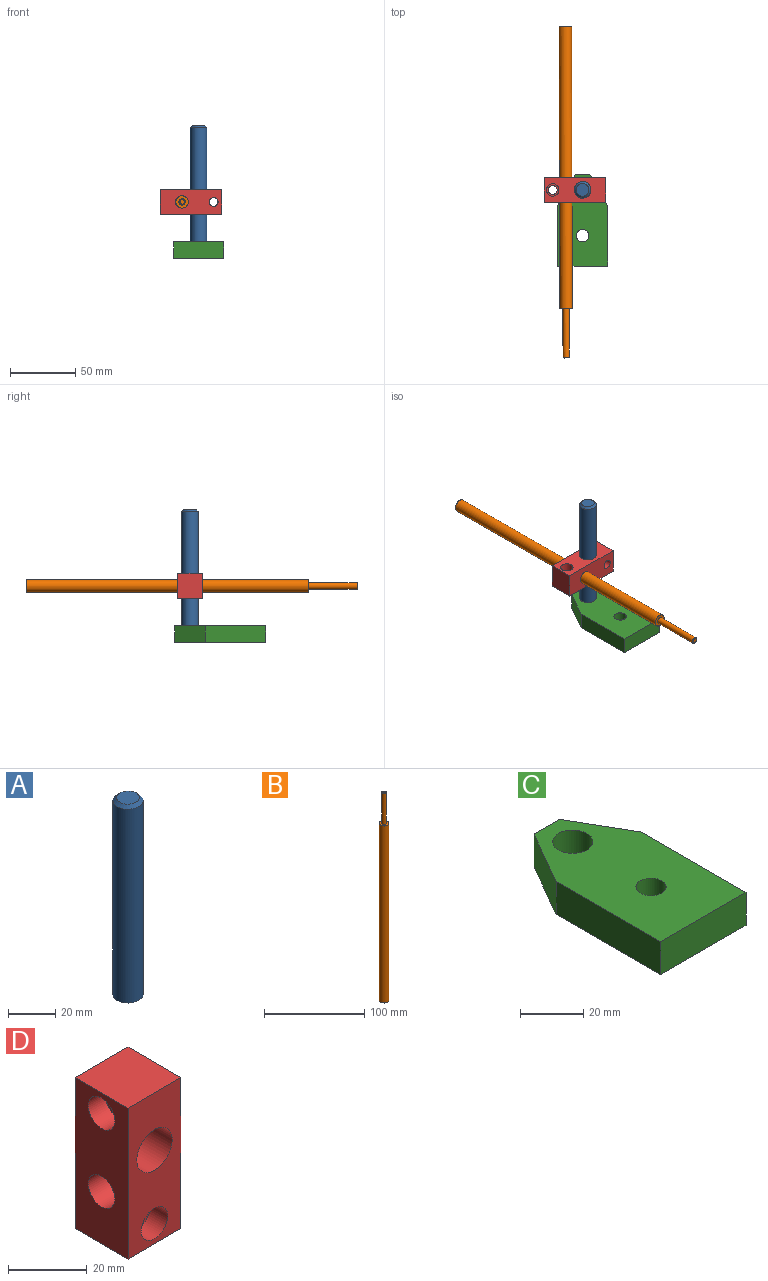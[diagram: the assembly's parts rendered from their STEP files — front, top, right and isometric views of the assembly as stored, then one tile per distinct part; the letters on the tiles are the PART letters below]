
ASSEMBLY  parts=4 mates=4
PART A: 4 faces, bbox 12.7x12.7x101.6 mm
  f0: cylinder r=6.35mm len=100.08mm, axis (0,0,-1), area 3992.9mm2, adj f2,f3
  f1: plane 9.65x9.65mm, normal (0,0,1), area 73.2mm2, adj f3
  f2: plane 12.7x12.7mm, normal (0,0,-1), area 126.7mm2, adj f0
  f3: cone r=4.83mm half-angle=45deg, axis (0,0,-1), area 75.7mm2, adj f0,f1
PART B: 6 faces, bbox 9.5x9.5x254 mm
  f0: cylinder r=4.76mm len=215.9mm, axis (0,0,-1), area 6460.5mm2, adj f1,f2
  f1: plane 9.53x9.53mm, normal (0,0,1), area 53.4mm2, adj f0,f3
  f2: plane 9.53x9.53mm, normal (0,0,-1), area 71.3mm2, adj f0
  f3: cylinder r=2.38mm len=37.47mm, axis (0,0,-1), area 560.5mm2, adj f1,f5
  f4: plane 3.49x3.49mm, normal (0,0,1), area 9.6mm2, adj f5
  f5: cone r=1.75mm half-angle=45deg, axis (0,0,-1), area 11.6mm2, adj f3,f4
PART C: 10 faces, bbox 38.1x69.8x12.7 mm
  f0: plane 46.57x12.7mm, normal (-1,0,0), area 591.4mm2, adj f1,f7,f8,f9
  f1: plane 38.1x12.7mm, normal (0,-1,0), area 483.9mm2, adj f0,f2,f8,f9
  f2: plane 46.57x12.7mm, normal (1,0,0), area 591.4mm2, adj f1,f3,f8,f9
  f3: plane 23.27x13.44mm, normal (0.87,0.5,0), area 341.3mm2, adj f2,f4,f8,f9
  f4: plane 12.7x11.23mm, normal (0,1,0), area 142.6mm2, adj f3,f7,f8,f9
  f5: cylinder r=4.76mm len=12.7mm, axis (0,0,-1), area 380mm2, adj f8,f9
  f6: cylinder r=6.35mm len=12.7mm, axis (0,0,-1), area 506.7mm2, adj f8,f9
  f7: plane 23.27x13.44mm, normal (-0.87,0.5,0), area 341.3mm2, adj f0,f4,f8,f9
  f8: plane 69.84x38.1mm, normal (0,0,1), area 2150.3mm2, adj f0,f1,f2,f3,f4,f5,f6,f7
  f9: plane 69.84x38.1mm, normal (0,0,-1), area 2150.3mm2, adj f0,f1,f2,f3,f4,f5,f6,f7
PART D: 14 faces, bbox 19.1x19.1x47 mm
  f0: plane 46.99x19.05mm, normal (0,1,0), area 732.6mm2, adj f1,f3,f4,f5,f6,f7
  f1: plane 46.99x19.05mm, normal (-1,0,0), area 752.6mm2, adj f0,f2,f4,f5,f10,f13
  f2: plane 46.99x19.05mm, normal (0,-1,0), area 697.2mm2, adj f1,f3,f4,f5,f6,f9
  f3: plane 46.99x19.05mm, normal (1,0,0), area 788.1mm2, adj f0,f2,f4,f5,f10,f11
  f4: plane 19.05x19.05mm, normal (0,0,1), area 362.9mm2, adj f0,f1,f2,f3
  f5: plane 19.05x19.05mm, normal (0,0,-1), area 362.9mm2, adj f0,f1,f2,f3
  f6: cylinder r=6.35mm len=19.05mm, axis (0,-1,0), area 760.1mm2, adj f0,f2
  f7: cylinder r=3.38mm len=12.9mm, axis (0,-1,0), area 273.9mm2, adj f0,f8
  f8: plane 9.53x9.53mm, normal (0,-1,0), area 35.4mm2, adj f7,f9
  f9: cylinder r=4.76mm len=9.53mm, axis (0,-1,0), area 183.9mm2, adj f2,f8
  f10: cylinder r=4.76mm len=19.05mm, axis (-1,0,0), area 570mm2, adj f1,f3
  f11: cylinder r=3.38mm len=12.9mm, axis (-1,0,0), area 273.9mm2, adj f3,f12
  f12: plane 9.53x9.53mm, normal (-1,0,0), area 35.4mm2, adj f11,f13
  f13: cylinder r=4.76mm len=9.53mm, axis (-1,0,0), area 183.9mm2, adj f1,f12
PLACE A t=(-164.05,-80.63,18.13)mm
PLACE B rot(axis=(0.43,0.64,-0.64),133deg) t=(-131.68,70.31,101.89)mm
PLACE C t=(-125.03,-73.54,18.13)mm fixed
PLACE D rot(axis=(-0.58,0.58,-0.58),119.9deg) t=(-154.12,-103.94,86.97)mm
MATE fastened C.f6 <-> A.f0  axis (0,0,-1) through (-125.03,-55.11,18.13)mm
MATE cylindrical B.f0 <-> D.f10  axis (0,1,0) through (-138.01,-37.65,61.34)mm
MATE cylindrical A.f0 <-> D.f6  axis (0,0,-1) through (-125.03,-55.11,68.17)mm
MATE fastened A.f0 <-> C.f6  axis (0,0,-1) through (-125.03,-55.11,18.13)mm
